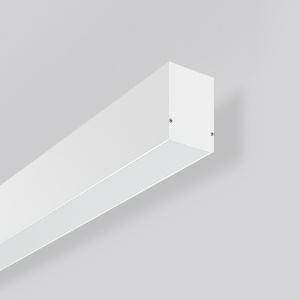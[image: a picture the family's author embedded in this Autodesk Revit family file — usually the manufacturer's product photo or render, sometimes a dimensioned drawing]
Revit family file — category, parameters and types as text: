
# Revit family: less_is_more_50_312606_002_76_2921
name_source: partatom
category: Lighting Fixtures
units: mm (PartAtom-declared; Revit-internal decimal feet)

## family parameters
Cut with Voids When Loaded = No
Host = Face
Light Source = No
Part Type = Normal
Room Calculation Point = No
Round Connector Dimension = Use Diameter
Shared = No

## types (1)
- LESS IS MORE 50 (1 x LED Modul 830, 1950 lm, 3000)
    Apparent Load = 16 VA
    CIE Flux Codes = 48 80 96 50 100
    Color Rendering = 80
    Color Temperature = 3000
    Default Elevation = 1800 mm
    Description = Series: LESS IS MORE 50
Linear wall luminaires. Housing: extruded aluminium profile, powder-coated. End cap aluminium powder-coated. Diffuser made of non-yellowing plastic (PMMA), opal. Direct 50%, indirect 50% light emission. Suitable for Wall (surface). LED unit with integrated converter interchangeable and removable. Suitable for through-wiring. With sensors or as a safety luminaire on request. 
Colour: traffic white, matt (RAL 9016)
Length: 847 mm
Width: 67 mm
Height: 75 mm
Lamp: LED
Socket: without socket
Colour temperature: 3000K
Colour rendering index (CRI): 80
Light source: LED
Socket lamp2: Without base
Colour temperature: 3000K
Colour rendering index (CRI) 2: 80
System power: 16 W
Rated luminous flux: 1950 lm
Luminous efficiency: 122 lm/W
Control gear: Converter, dimmable, DALI
Control gear: Converter, dimmable, DALI
Protection class: I
Type of protection: IP 20
    Height = 75 mm
    Lamp = 1 x LED Modul 830
    Lamp Light Flux = 1950 lm
    Lamp count = 1
    Length = 847 mm
    Lifetime = 50000 h
    Luminous efficacy = 122 lm/W
    Manufacturer = RZB
    ModVariant = No
    Model = 312606.002.76
    Mounting Place = Wall
    Mounting Type = Surface mounted
    Number of Poles = 1
    OnlyDefault = Yes
    Power Factor = 1
    Product Name = LESS IS MORE 50
    Product group = Surface mounted LED linear luminaires
    ProductGroupID = 2007
    Protection Class = Protection class I
    Protection Degree = IP 20
    RLX_Detail_Level = 1
    RLX_Emergency_Light_Flux = 0 lm
    RLX_Emergency_Type = 0
    RLX_Emergency_Type_DB = No
    RlxData = <blob elided: 39609 chars, md5=a2dcaae8>
    Socket = socket
    Standby Power = 0 W
    System Light Flux = 1950 lm
    System Power = 16 W
    Type Comments = Product without accessories
    Type Image = 312606.002.jpg
    URL = http://relux.com
    VarID = ---
    Voltage = 0 V
    Weight = 0.00 kg
    Width = 67 mm

## geometry (parser evidence)
native form markers: Blend x4, Sweep x14
no freeform markers — native parametric forms only
